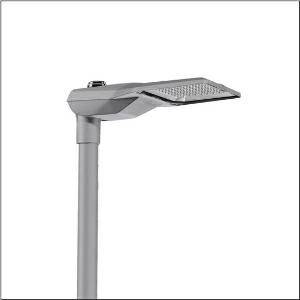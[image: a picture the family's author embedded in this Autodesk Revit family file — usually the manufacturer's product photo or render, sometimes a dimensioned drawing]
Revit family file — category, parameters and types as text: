
# Revit family: streetlight_sl_21_midi___st1_0a_5xe7d27n08mb_7be8
name_source: partatom
category: Lighting Fixtures
units: mm (PartAtom-declared; Revit-internal decimal feet)

## family parameters
Cut with Voids When Loaded = No
Host = Face
Light Source = No
Part Type = Normal
Room Calculation Point = No
Round Connector Dimension = Use Diameter
Shared = No

## types (1)
- --- (1 x LED, 14990 lm, 134.3 W, 2200K)
    Apparent Load = 134 VA
    CIE Flux Codes = 37 72 97 100 100
    Color Rendering = 70
    Color Temperature = 2200K
    Default Elevation = 1800 mm
    Description = Streetlight SL 21 midi, mast luminaire, primary light control with lens, of PMMA, primary optical cover: cover, of toughened safety glass, transparent, light distribution: ST1.0a, light emission: direct distribution, primary light characteristic: asymmetric, installation type: side-entry, LED, 3G 2.5mm², High Power LED, rated luminous flux: 14.990lm, luminous efficacy: 112lm/W, light colour: 722, colour temperature: 2200K, control: overheat protection, pre-setting: linear dimming characteristic, constant luminous flux control, time-dependent luminous flux control, flexible luminous flux parameterisation, mains connection: 220..240V, AC, 50/60Hz, connection cable pre-assembled, cable length: 12,5m, wiring characteristics: H05VV-F, start of lifetime: 134W, end of service life: 141W, reduction: 60W, luminaire housing, of diecast aluminium (EN AC-44300), powder-coated, Siteco® metallic grey (DB 702S), corrosivity category C5 mid according to DIN EN ISO 12944, multi-level sealing system, sealing non-destructively replaceable, inclination adjustable: 0°, 5°, 10°, 15°, length: 644mm, width: 335mm, height: 110mm, spigot size: 42mm (side-entry), protection rating (complete): IP66, insulation class (complete): insulation class I (protective earthing), certification: CE, ENEC, ENEC+, VDE, impact resistance: IK09, permissible operating ambient temperature for outdoor applications: -40..+50°C, standard-compliant lighting for roads and squares, packaging unit: 1 piece

Light Distribution: ST1.0a
    Height = 111 mm
    Lamp = 1 x LED
    Lamp Light Flux = 14990 lm
    Lamp Power = 134.3 W
    Lamp count = 1
    Length = 644 mm
    Luminous efficacy = 112 lm/W
    Manufacturer = Siteco
    ModVariant = No
    Model = 5XE7D27N08MB
    Number of Poles = 1
    OnlyDefault = Yes
    Power Factor = 1
    Product Name = Streetlight SL 21 midi | ST1.0a
    Product group = mast luminaire | pylon top
    ProductGroupID = 6100
    Protection Class = Protection class I
    Protection Degree = IP 66
    RLX_Detail_Level = 1
    RLX_Emergency_Light_Flux = 0 lm
    RLX_Emergency_Type = 0
    RLX_Emergency_Type_DB = No
    RlxData = <blob elided: 90221 chars, md5=4485581a>
    Socket = socket
    Standby Power = 0 W
    System Light Flux = 14991 lm
    System Power = 134 W
    Type Comments = factory setting: luminous flux: 100 % | dim-lin: 254 | 687 mA
    Type Image = l_1294377.jpg
    URL = http://relux.com
    VarID = @adj_105929
    Voltage = 0 V
    Weight = 0.00 kg
    Width = 336 mm

## geometry (parser evidence)
native form markers: Blend x4, Sweep x11
no freeform markers — native parametric forms only
